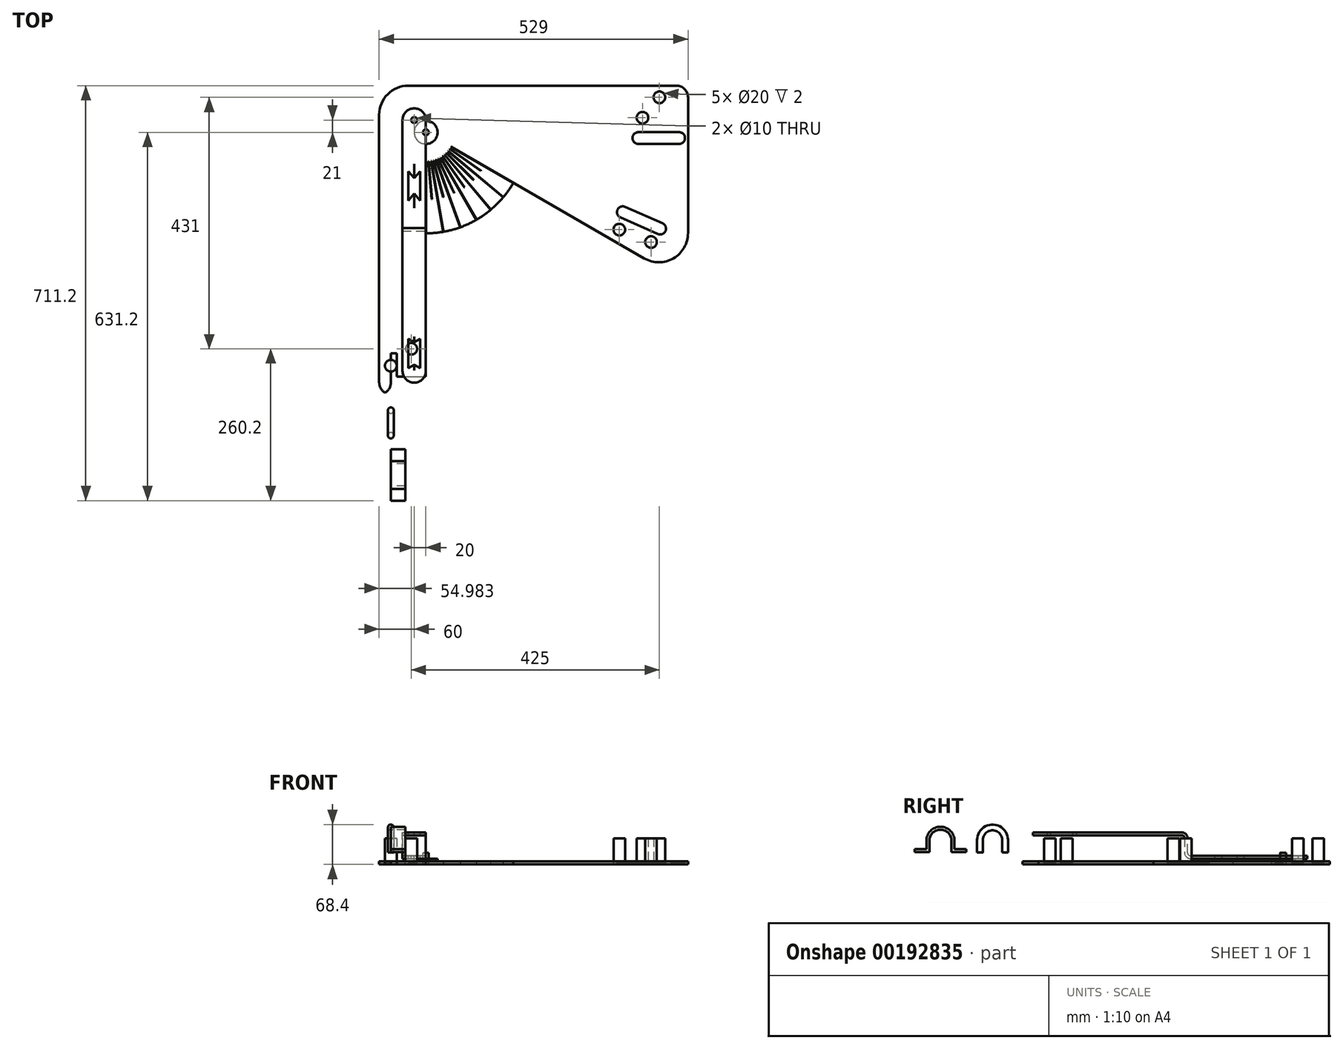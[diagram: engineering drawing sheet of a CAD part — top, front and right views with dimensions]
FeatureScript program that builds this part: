
annotation { "Feature Type Name" : "Feature", "Feature Type Description" : "" }
export const myFeature = defineFeature(function(context is Context, id is Id, definition is map)
    precondition{}
    {
        {
            var Q0;
            Q0=qCreatedBy(makeId("Top.planeOp"),FACE);
            var sketch = newSketch(context, id + "F0", { "sketchPlane" : qUnion([Q0])});
            skLineSegment(sketch, "E0.bottom", {"start": v(0, 0) * mm, "end": v(489, 0) * mm});
            skLineSegment(sketch, "E0.left", {"start": v(0, 0) * mm, "end": v(0, 500) * mm});
            skLineSegment(sketch, "E0.right", {"start": v(489, 0) * mm, "end": v(489, 479) * mm});
            skLineSegment(sketch, "E1.top", {"start": v(0, 0) * mm, "end": v(10, 0) * mm});
            skLineSegment(sketch, "E1.left", {"start": v(0, 489) * mm, "end": v(0, 0) * mm});
            skLineSegment(sketch, "E1.right", {"start": v(10, 50) * mm, "end": v(10, 10) * mm});
            skPoint(sketch, "E2", {"position": v(60, 429) * mm});
            skLineSegment(sketch, "E3", {"start": v(60, 255.9) * mm, "end": v(60, 0) * mm});
            skLineSegment(sketch, "E4", {"start": v(209.9, 342.45) * mm, "end": v(489, 181.32) * mm});
            skLineSegment(sketch, "E5.bottom", {"start": v(10, 48) * mm, "end": v(60, 48) * mm, "construction": true});
            skLineSegment(sketch, "E5.right", {"start": v(60, 48) * mm, "end": v(60, 10) * mm, "construction": true});
            skLineSegment(sketch, "E6.top", {"start": v(441, 429) * mm, "end": v(479, 429) * mm, "construction": true});
            skLineSegment(sketch, "E6.left", {"start": v(441, 479) * mm, "end": v(441, 429) * mm, "construction": true});
            skArc(sketch, "E7", {"start": v(60, 29) * mm, "mid": v(342.84, 146.16) * mm, "end": v(460, 429) * mm, "construction": true});
            skPoint(sketch, "E8", {"position": v(10, 29) * mm});
            skPoint(sketch, "E9", {"position": v(460, 479) * mm});
            skArc(sketch, "E10.0", {"start": v(60, 10) * mm, "mid": v(356.28, 132.72) * mm, "end": v(479, 429) * mm, "construction": true});
            skArc(sketch, "E11.0", {"start": v(60, 48) * mm, "mid": v(329.4, 159.6) * mm, "end": v(441, 429) * mm, "construction": true});
            skLineSegment(sketch, "E12", {"start": v(60, 255.9) * mm, "end": v(209.9, 342.45) * mm, "construction": true});
            skPoint(sketch, "E13.end.orphan", {"position": v(189.9, 354) * mm});
            skPoint(sketch, "E13.start.orphan", {"position": v(60, 279) * mm});
            skCircle(sketch, "E14", {"center": v(60, 429) * mm, "radius": 5 * mm});
            skLineSegment(sketch, "E15.top", {"start": v(489, 489) * mm, "end": v(0, 489) * mm});
            skLineSegment(sketch, "E15.left", {"start": v(489, 479) * mm, "end": v(489, 489) * mm});
            skLineSegment(sketch, "E16", {"start": v(439, 489) * mm, "end": v(439, 479) * mm});
            skLineSegment(sketch, "E17", {"start": v(439, 479) * mm, "end": v(479, 479) * mm});
            skLineSegment(sketch, "E18", {"start": v(479, 479) * mm, "end": v(479, 429) * mm});
            skLineSegment(sketch, "E19", {"start": v(489, 429) * mm, "end": v(479, 429) * mm});
            skArc(sketch, "E20", {"start": v(60, 255.9) * mm, "mid": v(146.55, 279.1) * mm, "end": v(209.9, 342.45) * mm});
            skLineSegment(sketch, "E21", {"start": v(0, 50) * mm, "end": v(10, 50) * mm});
            skLineSegment(sketch, "E22", {"start": v(10, 10) * mm, "end": v(60, 10) * mm});
            skLineSegment(sketch, "E23", {"start": v(60, 0) * mm, "end": v(60, -20) * mm});
            skLineSegment(sketch, "E24", {"start": v(60, -20) * mm, "end": v(0, -20) * mm});
            skLineSegment(sketch, "E25", {"start": v(0, -20) * mm, "end": v(0, 0) * mm});
            skLineSegment(sketch, "E26", {"start": v(0, 489) * mm, "end": v(-20, 489) * mm});
            skLineSegment(sketch, "E27", {"start": v(-20, 489) * mm, "end": v(-20, -20) * mm});
            skLineSegment(sketch, "E28", {"start": v(-20, -20) * mm, "end": v(0, -20) * mm});
            skLineSegment(sketch, "E29", {"start": v(489, 181.32) * mm, "end": v(509, 169.77) * mm});
            skLineSegment(sketch, "E30", {"start": v(509, 169.77) * mm, "end": v(509, 489) * mm});
            skLineSegment(sketch, "E31", {"start": v(509, 489) * mm, "end": v(489, 489) * mm});
            skLineSegment(sketch, "E32", {"start": v(509, 489) * mm, "end": v(509, 509) * mm});
            skLineSegment(sketch, "E33", {"start": v(509, 509) * mm, "end": v(-20, 509) * mm});
            skLineSegment(sketch, "E34", {"start": v(-20, 509) * mm, "end": v(-20, 489) * mm});
            skSolve(sketch);
        }
        {
            var Q0;
            {var subQ3=sQuery(id+"F0.wireOp",EDGE,"E1.right");Q0=makeQuery(id+"F0.imprint","IMPRINT",FACE,{"disambiguationData":[TD([[makeQuery(id+"F0.imprint","IMPRINT",EDGE,{"derivedFrom":subQ3}),1.0]])]});}
            var Q1;
            {var subQ2=sQuery(id+"F0.wireOp",EDGE,"E1.top");Q1=makeQuery(id+"F0.imprint","IMPRINT",FACE,{"disambiguationData":[TD([[makeQuery(id+"F0.imprint","IMPRINT",EDGE,{"derivedFrom":subQ2}),1.0]])]});}
            var Q2;
            {var subQ1=sQuery(id+"F0.wireOp",EDGE,"E15.left");Q2=makeQuery(id+"F0.imprint","IMPRINT",FACE,{"disambiguationData":[TD([[makeQuery(id+"F0.imprint","IMPRINT",EDGE,{"derivedFrom":subQ1}),1.0]])]});}
            var Q3;
            {var subQ1=sQuery(id+"F0.wireOp",EDGE,"E25");Q3=makeQuery(id+"F0.imprint","IMPRINT",FACE,{"disambiguationData":[TD([[makeQuery(id+"F0.imprint","IMPRINT",EDGE,{"derivedFrom":subQ1}),1.0]])]});}
            var Q4;
            {var subQ0=sQuery(id+"F0.wireOp",EDGE,"E1.top");Q4=makeQuery(id+"F0.imprint","IMPRINT",FACE,{"disambiguationData":[TD([[makeQuery(id+"F0.imprint","IMPRINT",EDGE,{"derivedFrom":subQ0}),-1.0]])]});}
            var Q5;
            {var subQ3=sQuery(id+"F0.wireOp",EDGE,"E26");Q5=makeQuery(id+"F0.imprint","IMPRINT",FACE,{"disambiguationData":[TD([[makeQuery(id+"F0.imprint","IMPRINT",EDGE,{"derivedFrom":subQ3}),-1.0]])]});}
            var Q6;
            {var subQ1=sQuery(id+"F0.wireOp",EDGE,"E15.left");Q6=makeQuery(id+"F0.imprint","IMPRINT",FACE,{"disambiguationData":[TD([[makeQuery(id+"F0.imprint","IMPRINT",EDGE,{"derivedFrom":subQ1}),-1.0]])]});}
            extrude(context, id + "F1", {"entities" : qUnion([Q0, Q1, Q2, Q3, Q4, Q5, Q6]), "depth" : 5 * mm});
        }
        {
            var Q0;
            Q0=makeQuery(id+"F1.opExtrude","SWEPT_FACE",FACE,{"disambiguationData":[OSD([sQuery(id+"F0.wireOp",EDGE,"E33")])]});
            cPlane(context, id + "F2", {"entities" : qUnion([Q0]), "cplaneType" : CPlaneType.OFFSET, "offset" : 80 * mm, "oppositeDirection" : true, "width" : 150 * mm, "height" : 150 * mm});
        }
        {
            var Q0;
            Q0=qCreatedBy(id+"F2.planeOp",FACE);
            var sketch = newSketch(context, id + "F3", { "sketchPlane" : qUnion([Q0])});
            skLineSegment(sketch, "E35", {"start": v(-60, 20) * mm, "end": v(-60, 0) * mm});
            skLineSegment(sketch, "E36", {"start": v(-60, 20) * mm, "end": v(-65, 20) * mm});
            skLineSegment(sketch, "E37", {"start": v(-65, 20) * mm, "end": v(-65, 10) * mm});
            skLineSegment(sketch, "E38", {"start": v(-65, 10) * mm, "end": v(-80, 10) * mm});
            skLineSegment(sketch, "E39", {"start": v(-80, 10) * mm, "end": v(-80, 5) * mm});
            skLineSegment(sketch, "E40", {"start": v(-80, 5) * mm, "end": v(-65, 5) * mm});
            skLineSegment(sketch, "E41", {"start": v(-65, 5) * mm, "end": v(-65, 0) * mm});
            skLineSegment(sketch, "E42", {"start": v(-65, 0) * mm, "end": v(-60, 0) * mm});
            skSolve(sketch);
        }
        {
            var Q0;
            Q0=qSketchRegion(id+"F3",true);
            var Q1;
            Q1=sQuery(id+"F3.wireOp",EDGE,"E35");
            revolve(context, id + "F4", {"entities" : qUnion([Q0]), "axis" : qUnion([Q1]), "revolveType" : RevolveType.FULL});
        }
        {
            var Q0;
            Q0=makeQuery(id+"F1.opExtrude","CAP_FACE",FACE,{"disambiguationData":[OSD([sQuery(id+"F0.wireOp",EDGE,"E0.bottom"),sQuery(id+"F0.wireOp",EDGE,"E0.top"),sQuery(id+"F0.wireOp",EDGE,"E0.right"),sQuery(id+"F0.wireOp",EDGE,"E1.right"),sQuery(id+"F0.wireOp",EDGE,"E3"),sQuery(id+"F0.wireOp",EDGE,"E4"),sQuery(id+"F0.wireOp",EDGE,"E12"),sQuery(id+"F0.wireOp",EDGE,"E14")])],"isStart":false});
            cPlane(context, id + "F5", {"entities" : qUnion([Q0]), "cplaneType" : CPlaneType.OFFSET, "offset" : 0 * mm, "width" : 150 * mm, "height" : 150 * mm});
        }
        {
            var Q0;
            Q0=qCreatedBy(id+"F5.planeOp",FACE);
            var sketch = newSketch(context, id + "F6", { "sketchPlane" : qUnion([Q0])});
            skCircle(sketch, "E43", {"center": v(34.98, 58) * mm, "radius": 10 * mm});
            skLineSegment(sketch, "E44.bottom", {"start": v(9.98, 10) * mm, "end": v(59.98, 10) * mm, "construction": true});
            skLineSegment(sketch, "E44.top", {"start": v(9.98, 48) * mm, "end": v(59.98, 48) * mm, "construction": true});
            skLineSegment(sketch, "E44.left", {"start": v(9.98, 10) * mm, "end": v(9.98, 48) * mm, "construction": true});
            skLineSegment(sketch, "E44.right", {"start": v(59.98, 10) * mm, "end": v(59.98, 48) * mm, "construction": true});
            skLineSegment(sketch, "E45.bottom", {"start": v(478.98, 479) * mm, "end": v(440.98, 479) * mm, "construction": true});
            skLineSegment(sketch, "E45.top", {"start": v(478.98, 429) * mm, "end": v(440.98, 429) * mm, "construction": true});
            skLineSegment(sketch, "E45.left", {"start": v(478.98, 479) * mm, "end": v(478.98, 429) * mm, "construction": true});
            skLineSegment(sketch, "E45.right", {"start": v(440.98, 479) * mm, "end": v(440.98, 429) * mm, "construction": true});
            skArc(sketch, "E46", {"start": v(59.98, 29) * mm, "mid": v(342.83, 146.16) * mm, "end": v(459.98, 429) * mm, "construction": true});
            skArc(sketch, "E47.0", {"start": v(59.98, 10) * mm, "mid": v(356.26, 132.72) * mm, "end": v(478.98, 429) * mm, "construction": true});
            skArc(sketch, "E48.0", {"start": v(59.98, 48) * mm, "mid": v(329.4, 159.6) * mm, "end": v(440.98, 429) * mm, "construction": true});
            skLineSegment(sketch, "E49", {"start": v(459.98, 429) * mm, "end": v(459.98, 479) * mm, "construction": true});
            skLineSegment(sketch, "E50", {"start": v(59.98, 29) * mm, "end": v(9.98, 29) * mm, "construction": true});
            skCircle(sketch, "E51", {"center": v(430.98, 454) * mm, "radius": 10 * mm});
            skCircle(sketch, "E52", {"center": v(445.6, 241.01) * mm, "radius": 10 * mm});
            skLineSegment(sketch, "E53", {"start": v(445.6, 241.01) * mm, "end": v(391.37, 262.2) * mm, "construction": true});
            skCircle(sketch, "E54", {"center": v(391.37, 262.2) * mm, "radius": 10 * mm});
            skCircle(sketch, "E55.MirrorC", {"center": v(34.98, 0) * mm, "radius": 10 * mm});
            skCircle(sketch, "E56", {"center": v(-0.02, 29) * mm, "radius": 10 * mm});
            skLineSegment(sketch, "E57", {"start": v(34.98, 0) * mm, "end": v(34.98, 48) * mm, "construction": true});
            skCircle(sketch, "E58.MirrorC", {"center": v(488.98, 454) * mm, "radius": 10 * mm});
            skLineSegment(sketch, "E59", {"start": v(430.98, 454) * mm, "end": v(488.98, 454) * mm, "construction": true});
            skCircle(sketch, "E60", {"center": v(459.98, 489) * mm, "radius": 10 * mm});
            skSolve(sketch);
        }
        {
            var Q0;
            Q0=makeQuery(id+"F6.imprint","IMPRINT",FACE,{"disambiguationData":[TD([[makeQuery(id+"F6.imprint","IMPRINT",EDGE,{"derivedFrom":sQuery(id+"F6.wireOp",EDGE,"E58.MirrorC")}),-1.0]])]});
            var Q1;
            Q1=makeQuery(id+"F6.imprint","IMPRINT",FACE,{"disambiguationData":[TD([[makeQuery(id+"F6.imprint","IMPRINT",EDGE,{"derivedFrom":sQuery(id+"F6.wireOp",EDGE,"E60")}),1.0]])]});
            var Q2;
            Q2=makeQuery(id+"F6.imprint","IMPRINT",FACE,{"disambiguationData":[TD([[makeQuery(id+"F6.imprint","IMPRINT",EDGE,{"derivedFrom":sQuery(id+"F6.wireOp",EDGE,"E51")}),1.0]])]});
            var Q3;
            Q3=makeQuery(id+"F6.imprint","IMPRINT",FACE,{"disambiguationData":[TD([[makeQuery(id+"F6.imprint","IMPRINT",EDGE,{"derivedFrom":sQuery(id+"F6.wireOp",EDGE,"E52")}),1.0]])]});
            var Q4;
            Q4=makeQuery(id+"F6.imprint","IMPRINT",FACE,{"disambiguationData":[TD([[makeQuery(id+"F6.imprint","IMPRINT",EDGE,{"derivedFrom":sQuery(id+"F6.wireOp",EDGE,"E54")}),1.0]])]});
            var Q5;
            Q5=makeQuery(id+"F6.imprint","IMPRINT",FACE,{"disambiguationData":[TD([[makeQuery(id+"F6.imprint","IMPRINT",EDGE,{"derivedFrom":sQuery(id+"F6.wireOp",EDGE,"E55.MirrorC")}),-1.0]])]});
            var Q6;
            Q6=makeQuery(id+"F6.imprint","IMPRINT",FACE,{"disambiguationData":[TD([[makeQuery(id+"F6.imprint","IMPRINT",EDGE,{"derivedFrom":sQuery(id+"F6.wireOp",EDGE,"E43")}),1.0]])]});
            var Q7;
            Q7=makeQuery(id+"F6.imprint","IMPRINT",FACE,{"disambiguationData":[TD([[makeQuery(id+"F6.imprint","IMPRINT",EDGE,{"derivedFrom":sQuery(id+"F6.wireOp",EDGE,"E56")}),1.0]])]});
            extrude(context, id + "F7", {"entities" : qUnion([Q0, Q1, Q2, Q3, Q4, Q5, Q6, Q7]), "operationType" : NewBodyOperationType.REMOVE, "oppositeDirection" : true, "depth" : 2 * mm});
        }
        {
            var Q0;
            Q0=makeQuery(id+"F6.imprint","IMPRINT",FACE,{"disambiguationData":[TD([[makeQuery(id+"F6.imprint","IMPRINT",EDGE,{"derivedFrom":sQuery(id+"F6.wireOp",EDGE,"E58.MirrorC")}),-1.0]])]});
            var Q1;
            Q1=makeQuery(id+"F6.imprint","IMPRINT",FACE,{"disambiguationData":[TD([[makeQuery(id+"F6.imprint","IMPRINT",EDGE,{"derivedFrom":sQuery(id+"F6.wireOp",EDGE,"E60")}),1.0]])]});
            var Q2;
            Q2=makeQuery(id+"F6.imprint","IMPRINT",FACE,{"disambiguationData":[TD([[makeQuery(id+"F6.imprint","IMPRINT",EDGE,{"derivedFrom":sQuery(id+"F6.wireOp",EDGE,"E51")}),1.0]])]});
            var Q3;
            Q3=makeQuery(id+"F6.imprint","IMPRINT",FACE,{"disambiguationData":[TD([[makeQuery(id+"F6.imprint","IMPRINT",EDGE,{"derivedFrom":sQuery(id+"F6.wireOp",EDGE,"E52")}),1.0]])]});
            var Q4;
            Q4=makeQuery(id+"F6.imprint","IMPRINT",FACE,{"disambiguationData":[TD([[makeQuery(id+"F6.imprint","IMPRINT",EDGE,{"derivedFrom":sQuery(id+"F6.wireOp",EDGE,"E54")}),1.0]])]});
            var Q5;
            Q5=makeQuery(id+"F6.imprint","IMPRINT",FACE,{"disambiguationData":[TD([[makeQuery(id+"F6.imprint","IMPRINT",EDGE,{"derivedFrom":sQuery(id+"F6.wireOp",EDGE,"E56")}),1.0]])]});
            var Q6;
            Q6=makeQuery(id+"F6.imprint","IMPRINT",FACE,{"disambiguationData":[TD([[makeQuery(id+"F6.imprint","IMPRINT",EDGE,{"derivedFrom":sQuery(id+"F6.wireOp",EDGE,"E55.MirrorC")}),-1.0]])]});
            var Q7;
            Q7=makeQuery(id+"F6.imprint","IMPRINT",FACE,{"disambiguationData":[TD([[makeQuery(id+"F6.imprint","IMPRINT",EDGE,{"derivedFrom":sQuery(id+"F6.wireOp",EDGE,"E43")}),1.0]])]});
            extrude(context, id + "F8", {"entities" : qUnion([Q0, Q1, Q2, Q3, Q4, Q5, Q6, Q7]), "depth" : 40 * mm});
        }
        {
            var Q0;
            Q0=makeQuery(id+"F1.opExtrude","CAP_FACE",FACE,{"disambiguationData":[OSD([sQuery(id+"F0.wireOp",EDGE,"E0.bottom"),sQuery(id+"F0.wireOp",EDGE,"E0.right"),sQuery(id+"F0.wireOp",EDGE,"E1.right"),sQuery(id+"F0.wireOp",EDGE,"E3"),sQuery(id+"F0.wireOp",EDGE,"E4"),sQuery(id+"F0.wireOp",EDGE,"E12"),sQuery(id+"F0.wireOp",EDGE,"E14"),sQuery(id+"F0.wireOp",EDGE,"E15.top"),sQuery(id+"F0.wireOp",EDGE,"E16"),sQuery(id+"F0.wireOp",EDGE,"E17"),sQuery(id+"F0.wireOp",EDGE,"E18"),sQuery(id+"F0.wireOp",EDGE,"E19")])],"isStart":false});
            var sketch = newSketch(context, id + "F9", { "sketchPlane" : qUnion([Q0])});
            skLineSegment(sketch, "E61", {"start": v(60, 379) * mm, "end": v(60, 255.9) * mm});
            skLineSegment(sketch, "E62", {"start": v(103.3, 404) * mm, "end": v(209.9, 342.45) * mm});
            skArc(sketch, "E63", {"start": v(60, 314) * mm, "mid": v(117.5, 329.4) * mm, "end": v(159.6, 371.5) * mm});
            skLineSegment(sketch, "E64.0", {"start": v(64.45, 426.72) * mm, "end": v(210.03, 342.67) * mm});
            skArc(sketch, "E65", {"start": v(60, 424) * mm, "mid": v(62.6, 424.73) * mm, "end": v(64.45, 426.72) * mm});
            skLineSegment(sketch, "E66.trimOffspring", {"start": v(64.2, 426.29) * mm, "end": v(64.83, 425.92) * mm});
            skLineSegment(sketch, "E67", {"start": v(210.03, 342.67) * mm, "end": v(209.9, 342.45) * mm});
            skLineSegment(sketch, "E68", {"start": v(100.96, 400.32) * mm, "end": v(154.2, 363.04) * mm});
            skLineSegment(sketch, "E69", {"start": v(98.3, 396.86) * mm, "end": v(192.6, 317.74) * mm});
            skLineSegment(sketch, "E70", {"start": v(95.36, 393.64) * mm, "end": v(141.32, 347.68) * mm});
            skLineSegment(sketch, "E71", {"start": v(92.14, 390.7) * mm, "end": v(171.26, 296.4) * mm});
            skLineSegment(sketch, "E72", {"start": v(88.68, 388.04) * mm, "end": v(125.96, 334.8) * mm});
            skLineSegment(sketch, "E73", {"start": v(85, 385.7) * mm, "end": v(146.55, 279.1) * mm});
            skLineSegment(sketch, "E74", {"start": v(81.13, 383.68) * mm, "end": v(108.6, 324.77) * mm});
            skLineSegment(sketch, "E75", {"start": v(77.1, 382.02) * mm, "end": v(119.2, 266.34) * mm});
            skLineSegment(sketch, "E76", {"start": v(72.94, 380.7) * mm, "end": v(89.76, 317.92) * mm});
            skLineSegment(sketch, "E77", {"start": v(68.68, 379.76) * mm, "end": v(90.06, 258.54) * mm});
            skLineSegment(sketch, "E78", {"start": v(64.36, 379.2) * mm, "end": v(70.02, 314.44) * mm});
            skArc(sketch, "E79", {"start": v(60, 255.9) * mm, "mid": v(146.55, 279.1) * mm, "end": v(209.9, 342.45) * mm, "construction": true});
            skPoint(sketch, "E80.orphan", {"position": v(117.5, 329.4) * mm});
            skLineSegment(sketch, "E81.0", {"start": v(64.24, 426.34) * mm, "end": v(64.83, 425.92) * mm});
            skLineSegment(sketch, "E82.0", {"start": v(63.95, 425.93) * mm, "end": v(64.55, 425.51) * mm});
            skLineSegment(sketch, "E83.0", {"start": v(63.67, 425.6) * mm, "end": v(64.23, 425.13) * mm});
            skLineSegment(sketch, "E84.0", {"start": v(64, 425.98) * mm, "end": v(64.55, 425.51) * mm});
            skLineSegment(sketch, "E85.0", {"start": v(63.36, 425.29) * mm, "end": v(63.87, 424.77) * mm});
            skLineSegment(sketch, "E86.0", {"start": v(63.71, 425.64) * mm, "end": v(64.23, 425.13) * mm});
            skLineSegment(sketch, "E87.0", {"start": v(63.02, 425) * mm, "end": v(63.49, 424.45) * mm});
            skLineSegment(sketch, "E88.0", {"start": v(63.4, 425.33) * mm, "end": v(63.87, 424.77) * mm});
            skLineSegment(sketch, "E89.0", {"start": v(63.07, 425.05) * mm, "end": v(63.49, 424.45) * mm});
            skLineSegment(sketch, "E90.0", {"start": v(62.66, 424.76) * mm, "end": v(63.08, 424.17) * mm});
            skLineSegment(sketch, "E91.0", {"start": v(55.7, 435.96) * mm, "end": v(62.65, 423.92) * mm});
            skLineSegment(sketch, "E92.0", {"start": v(56.12, 436.21) * mm, "end": v(63.08, 424.17) * mm});
            skLineSegment(sketch, "E93.0", {"start": v(61.89, 424.36) * mm, "end": v(62.2, 423.7) * mm});
            skLineSegment(sketch, "E94.0", {"start": v(62.34, 424.57) * mm, "end": v(62.65, 423.92) * mm});
            skLineSegment(sketch, "E95.0", {"start": v(61.48, 424.22) * mm, "end": v(61.72, 423.53) * mm});
            skLineSegment(sketch, "E96.0", {"start": v(61.95, 424.39) * mm, "end": v(62.2, 423.7) * mm});
            skLineSegment(sketch, "E97.0", {"start": v(61.05, 424.1) * mm, "end": v(61.24, 423.4) * mm});
            skLineSegment(sketch, "E98.0", {"start": v(61.54, 424.24) * mm, "end": v(61.72, 423.53) * mm});
            skLineSegment(sketch, "E99.0", {"start": v(60.62, 424.03) * mm, "end": v(60.75, 423.32) * mm});
            skLineSegment(sketch, "E100.0", {"start": v(61.11, 424.12) * mm, "end": v(61.24, 423.4) * mm});
            skLineSegment(sketch, "E101.0", {"start": v(60.19, 424) * mm, "end": v(60.25, 423.27) * mm});
            skLineSegment(sketch, "E102.0", {"start": v(60.68, 424.04) * mm, "end": v(60.75, 423.32) * mm});
            skLineSegment(sketch, "E103.0", {"start": v(59.75, 429) * mm, "end": v(59.75, 255.9) * mm});
            skLineSegment(sketch, "E104.0", {"start": v(60.25, 424) * mm, "end": v(60.25, 423.27) * mm});
            skArc(sketch, "E105", {"start": v(103.3, 404) * mm, "mid": v(85, 385.7) * mm, "end": v(60, 379) * mm});
            skLineSegment(sketch, "E106.trimOffspring", {"start": v(60.25, 379) * mm, "end": v(60.25, 255.9) * mm});
            skLineSegment(sketch, "E107.trimOffspring", {"start": v(64.1, 379.17) * mm, "end": v(69.77, 314.42) * mm});
            skLineSegment(sketch, "E108.trimOffspring", {"start": v(64.6, 379.21) * mm, "end": v(70.27, 314.46) * mm});
            skLineSegment(sketch, "E109.trimOffspring", {"start": v(68.44, 379.72) * mm, "end": v(89.81, 258.5) * mm});
            skLineSegment(sketch, "E110.trimOffspring", {"start": v(68.93, 379.8) * mm, "end": v(90.3, 258.58) * mm});
            skLineSegment(sketch, "E111.trimOffspring", {"start": v(72.7, 380.64) * mm, "end": v(89.52, 317.85) * mm});
            skLineSegment(sketch, "E112.trimOffspring", {"start": v(73.18, 380.77) * mm, "end": v(90, 317.98) * mm});
            skLineSegment(sketch, "E113.trimOffspring", {"start": v(76.87, 381.93) * mm, "end": v(118.97, 266.26) * mm});
            skLineSegment(sketch, "E114.trimOffspring", {"start": v(77.34, 382.1) * mm, "end": v(119.44, 266.43) * mm});
            skLineSegment(sketch, "E115.trimOffspring", {"start": v(80.9, 383.58) * mm, "end": v(108.37, 324.67) * mm});
            skLineSegment(sketch, "E116.trimOffspring", {"start": v(81.36, 383.8) * mm, "end": v(108.83, 324.88) * mm});
            skLineSegment(sketch, "E117.trimOffspring", {"start": v(88.47, 387.9) * mm, "end": v(125.76, 334.65) * mm});
            skLineSegment(sketch, "E118.trimOffspring", {"start": v(88.88, 388.19) * mm, "end": v(126.17, 334.94) * mm});
            skLineSegment(sketch, "E119.trimOffspring", {"start": v(84.78, 385.57) * mm, "end": v(146.33, 278.97) * mm});
            skLineSegment(sketch, "E120.trimOffspring", {"start": v(85.22, 385.82) * mm, "end": v(146.76, 279.22) * mm});
            skLineSegment(sketch, "E121.trimOffspring", {"start": v(91.95, 390.54) * mm, "end": v(171.07, 296.24) * mm});
            skLineSegment(sketch, "E122.trimOffspring", {"start": v(92.33, 390.86) * mm, "end": v(171.45, 296.56) * mm});
            skLineSegment(sketch, "E123.trimOffspring", {"start": v(95.18, 393.47) * mm, "end": v(141.14, 347.5) * mm});
            skLineSegment(sketch, "E124.trimOffspring", {"start": v(95.53, 393.82) * mm, "end": v(141.5, 347.86) * mm});
            skLineSegment(sketch, "E125.trimOffspring", {"start": v(98.14, 396.67) * mm, "end": v(192.44, 317.55) * mm});
            skLineSegment(sketch, "E126.trimOffspring", {"start": v(98.46, 397.05) * mm, "end": v(192.76, 317.93) * mm});
            skLineSegment(sketch, "E127.trimOffspring", {"start": v(100.81, 400.12) * mm, "end": v(154.06, 362.83) * mm});
            skLineSegment(sketch, "E128.trimOffspring", {"start": v(101.1, 400.53) * mm, "end": v(154.35, 363.24) * mm});
            skLineSegment(sketch, "E129.trimOffspring", {"start": v(103.18, 403.78) * mm, "end": v(209.78, 342.24) * mm});
            skArc(sketch, "E130", {"start": v(209.9, 342.45) * mm, "mid": v(146.55, 279.1) * mm, "end": v(60, 255.9) * mm});
            skSolve(sketch);
        }
        {
            var Q0;
            {var subQ0=sQuery(id+"F9.wireOp",EDGE,"E105");var subQ1=sQuery(id+"F9.wireOp",EDGE,"E62");var subQ2=makeQuery(id+"F9.imprint","INTERSECT",VERTEX,{"derivedFrom":[subQ1,subQ0]});Q0=makeQuery(id+"F9.imprint","IMPRINT",FACE,{"disambiguationData":[TD([[makeQuery(id+"F9.imprint","IMPRINT",EDGE,{"disambiguationData":[TD([[subQ2,-1.0]])],"derivedFrom":subQ1}),-1.0]])]});}
            var Q1;
            {var subQ0=sQuery(id+"F9.wireOp",EDGE,"E62");var subQ3=sQuery(id+"F9.wireOp",EDGE,"E63");var subQ4=makeQuery(id+"F9.imprint","INTERSECT",VERTEX,{"derivedFrom":[subQ0,subQ3]});Q1=makeQuery(id+"F9.imprint","IMPRINT",FACE,{"disambiguationData":[TD([[makeQuery(id+"F9.imprint","IMPRINT",EDGE,{"disambiguationData":[TD([[subQ4,1.0]])],"derivedFrom":subQ3}),-1.0]])]});}
            var Q2;
            {var subQ0=sQuery(id+"F9.wireOp",EDGE,"E68");Q2=makeQuery(id+"F9.imprint","IMPRINT",FACE,{"disambiguationData":[TD([[makeQuery(id+"F9.imprint","IMPRINT",EDGE,{"derivedFrom":subQ0}),1.0]])]});}
            var Q3;
            {var subQ0=sQuery(id+"F9.wireOp",EDGE,"E68");Q3=makeQuery(id+"F9.imprint","IMPRINT",FACE,{"disambiguationData":[TD([[makeQuery(id+"F9.imprint","IMPRINT",EDGE,{"derivedFrom":subQ0}),-1.0]])]});}
            var Q4;
            {var subQ0=sQuery(id+"F9.wireOp",EDGE,"E69");var subQ1=sQuery(id+"F9.wireOp",EDGE,"E63");var subQ2=makeQuery(id+"F9.imprint","INTERSECT",VERTEX,{"derivedFrom":[subQ1,subQ0]});Q4=makeQuery(id+"F9.imprint","IMPRINT",FACE,{"disambiguationData":[TD([[makeQuery(id+"F9.imprint","IMPRINT",EDGE,{"disambiguationData":[TD([[subQ2,-1.0]])],"derivedFrom":subQ1}),1.0]])]});}
            var Q5;
            {var subQ0=sQuery(id+"F9.wireOp",EDGE,"E125.trimOffspring");var subQ1=sQuery(id+"F9.wireOp",EDGE,"E63");var subQ2=makeQuery(id+"F9.imprint","INTERSECT",VERTEX,{"derivedFrom":[subQ1,subQ0]});Q5=makeQuery(id+"F9.imprint","IMPRINT",FACE,{"disambiguationData":[TD([[makeQuery(id+"F9.imprint","IMPRINT",EDGE,{"disambiguationData":[TD([[subQ2,-1.0]])],"derivedFrom":subQ1}),1.0]])]});}
            var Q6;
            {var subQ0=sQuery(id+"F9.wireOp",EDGE,"E125.trimOffspring");var subQ1=sQuery(id+"F9.wireOp",EDGE,"E63");var subQ2=makeQuery(id+"F9.imprint","INTERSECT",VERTEX,{"derivedFrom":[subQ1,subQ0]});Q6=makeQuery(id+"F9.imprint","IMPRINT",FACE,{"disambiguationData":[TD([[makeQuery(id+"F9.imprint","IMPRINT",EDGE,{"disambiguationData":[TD([[subQ2,-1.0]])],"derivedFrom":subQ1}),-1.0]])]});}
            var Q7;
            {var subQ0=sQuery(id+"F9.wireOp",EDGE,"E69");var subQ1=sQuery(id+"F9.wireOp",EDGE,"E63");var subQ2=makeQuery(id+"F9.imprint","INTERSECT",VERTEX,{"derivedFrom":[subQ1,subQ0]});Q7=makeQuery(id+"F9.imprint","IMPRINT",FACE,{"disambiguationData":[TD([[makeQuery(id+"F9.imprint","IMPRINT",EDGE,{"disambiguationData":[TD([[subQ2,-1.0]])],"derivedFrom":subQ1}),-1.0]])]});}
            var Q8;
            {var subQ0=sQuery(id+"F9.wireOp",EDGE,"E70");Q8=makeQuery(id+"F9.imprint","IMPRINT",FACE,{"disambiguationData":[TD([[makeQuery(id+"F9.imprint","IMPRINT",EDGE,{"derivedFrom":subQ0}),-1.0]])]});}
            var Q9;
            {var subQ0=sQuery(id+"F9.wireOp",EDGE,"E70");Q9=makeQuery(id+"F9.imprint","IMPRINT",FACE,{"disambiguationData":[TD([[makeQuery(id+"F9.imprint","IMPRINT",EDGE,{"derivedFrom":subQ0}),1.0]])]});}
            var Q10;
            {var subQ0=sQuery(id+"F9.wireOp",EDGE,"E71");var subQ1=sQuery(id+"F9.wireOp",EDGE,"E63");var subQ2=makeQuery(id+"F9.imprint","INTERSECT",VERTEX,{"derivedFrom":[subQ1,subQ0]});Q10=makeQuery(id+"F9.imprint","IMPRINT",FACE,{"disambiguationData":[TD([[makeQuery(id+"F9.imprint","IMPRINT",EDGE,{"disambiguationData":[TD([[subQ2,-1.0]])],"derivedFrom":subQ1}),1.0]])]});}
            var Q11;
            {var subQ0=sQuery(id+"F9.wireOp",EDGE,"E71");var subQ1=sQuery(id+"F9.wireOp",EDGE,"E63");var subQ2=makeQuery(id+"F9.imprint","INTERSECT",VERTEX,{"derivedFrom":[subQ1,subQ0]});Q11=makeQuery(id+"F9.imprint","IMPRINT",FACE,{"disambiguationData":[TD([[makeQuery(id+"F9.imprint","IMPRINT",EDGE,{"disambiguationData":[TD([[subQ2,-1.0]])],"derivedFrom":subQ1}),-1.0]])]});}
            var Q12;
            {var subQ0=sQuery(id+"F9.wireOp",EDGE,"E121.trimOffspring");var subQ1=sQuery(id+"F9.wireOp",EDGE,"E63");var subQ2=makeQuery(id+"F9.imprint","INTERSECT",VERTEX,{"derivedFrom":[subQ1,subQ0]});Q12=makeQuery(id+"F9.imprint","IMPRINT",FACE,{"disambiguationData":[TD([[makeQuery(id+"F9.imprint","IMPRINT",EDGE,{"disambiguationData":[TD([[subQ2,-1.0]])],"derivedFrom":subQ1}),-1.0]])]});}
            var Q13;
            {var subQ0=sQuery(id+"F9.wireOp",EDGE,"E121.trimOffspring");var subQ1=sQuery(id+"F9.wireOp",EDGE,"E63");var subQ2=makeQuery(id+"F9.imprint","INTERSECT",VERTEX,{"derivedFrom":[subQ1,subQ0]});Q13=makeQuery(id+"F9.imprint","IMPRINT",FACE,{"disambiguationData":[TD([[makeQuery(id+"F9.imprint","IMPRINT",EDGE,{"disambiguationData":[TD([[subQ2,-1.0]])],"derivedFrom":subQ1}),1.0]])]});}
            var Q14;
            {var subQ0=sQuery(id+"F9.wireOp",EDGE,"E72");Q14=makeQuery(id+"F9.imprint","IMPRINT",FACE,{"disambiguationData":[TD([[makeQuery(id+"F9.imprint","IMPRINT",EDGE,{"derivedFrom":subQ0}),1.0]])]});}
            var Q15;
            {var subQ0=sQuery(id+"F9.wireOp",EDGE,"E72");Q15=makeQuery(id+"F9.imprint","IMPRINT",FACE,{"disambiguationData":[TD([[makeQuery(id+"F9.imprint","IMPRINT",EDGE,{"derivedFrom":subQ0}),-1.0]])]});}
            var Q16;
            {var subQ0=sQuery(id+"F9.wireOp",EDGE,"E120.trimOffspring");var subQ1=sQuery(id+"F9.wireOp",EDGE,"E63");var subQ2=makeQuery(id+"F9.imprint","INTERSECT",VERTEX,{"derivedFrom":[subQ1,subQ0]});Q16=makeQuery(id+"F9.imprint","IMPRINT",FACE,{"disambiguationData":[TD([[makeQuery(id+"F9.imprint","IMPRINT",EDGE,{"disambiguationData":[TD([[subQ2,1.0]])],"derivedFrom":subQ1}),1.0]])]});}
            var Q17;
            {var subQ0=sQuery(id+"F9.wireOp",EDGE,"E119.trimOffspring");var subQ1=sQuery(id+"F9.wireOp",EDGE,"E63");var subQ2=makeQuery(id+"F9.imprint","INTERSECT",VERTEX,{"derivedFrom":[subQ1,subQ0]});Q17=makeQuery(id+"F9.imprint","IMPRINT",FACE,{"disambiguationData":[TD([[makeQuery(id+"F9.imprint","IMPRINT",EDGE,{"disambiguationData":[TD([[subQ2,-1.0]])],"derivedFrom":subQ1}),1.0]])]});}
            var Q18;
            {var subQ0=sQuery(id+"F9.wireOp",EDGE,"E74");Q18=makeQuery(id+"F9.imprint","IMPRINT",FACE,{"disambiguationData":[TD([[makeQuery(id+"F9.imprint","IMPRINT",EDGE,{"derivedFrom":subQ0}),-1.0]])]});}
            var Q19;
            {var subQ0=sQuery(id+"F9.wireOp",EDGE,"E74");Q19=makeQuery(id+"F9.imprint","IMPRINT",FACE,{"disambiguationData":[TD([[makeQuery(id+"F9.imprint","IMPRINT",EDGE,{"derivedFrom":subQ0}),1.0]])]});}
            var Q20;
            {var subQ0=sQuery(id+"F9.wireOp",EDGE,"E75");var subQ1=sQuery(id+"F9.wireOp",EDGE,"E63");var subQ2=makeQuery(id+"F9.imprint","INTERSECT",VERTEX,{"derivedFrom":[subQ1,subQ0]});Q20=makeQuery(id+"F9.imprint","IMPRINT",FACE,{"disambiguationData":[TD([[makeQuery(id+"F9.imprint","IMPRINT",EDGE,{"disambiguationData":[TD([[subQ2,-1.0]])],"derivedFrom":subQ1}),1.0]])]});}
            var Q21;
            {var subQ0=sQuery(id+"F9.wireOp",EDGE,"E113.trimOffspring");var subQ1=sQuery(id+"F9.wireOp",EDGE,"E63");var subQ2=makeQuery(id+"F9.imprint","INTERSECT",VERTEX,{"derivedFrom":[subQ1,subQ0]});Q21=makeQuery(id+"F9.imprint","IMPRINT",FACE,{"disambiguationData":[TD([[makeQuery(id+"F9.imprint","IMPRINT",EDGE,{"disambiguationData":[TD([[subQ2,-1.0]])],"derivedFrom":subQ1}),1.0]])]});}
            var Q22;
            {var subQ0=sQuery(id+"F9.wireOp",EDGE,"E113.trimOffspring");var subQ1=sQuery(id+"F9.wireOp",EDGE,"E63");var subQ2=makeQuery(id+"F9.imprint","INTERSECT",VERTEX,{"derivedFrom":[subQ1,subQ0]});Q22=makeQuery(id+"F9.imprint","IMPRINT",FACE,{"disambiguationData":[TD([[makeQuery(id+"F9.imprint","IMPRINT",EDGE,{"disambiguationData":[TD([[subQ2,-1.0]])],"derivedFrom":subQ1}),-1.0]])]});}
            var Q23;
            {var subQ0=sQuery(id+"F9.wireOp",EDGE,"E75");var subQ1=sQuery(id+"F9.wireOp",EDGE,"E63");var subQ2=makeQuery(id+"F9.imprint","INTERSECT",VERTEX,{"derivedFrom":[subQ1,subQ0]});Q23=makeQuery(id+"F9.imprint","IMPRINT",FACE,{"disambiguationData":[TD([[makeQuery(id+"F9.imprint","IMPRINT",EDGE,{"disambiguationData":[TD([[subQ2,-1.0]])],"derivedFrom":subQ1}),-1.0]])]});}
            var Q24;
            {var subQ0=sQuery(id+"F9.wireOp",EDGE,"E76");Q24=makeQuery(id+"F9.imprint","IMPRINT",FACE,{"disambiguationData":[TD([[makeQuery(id+"F9.imprint","IMPRINT",EDGE,{"derivedFrom":subQ0}),1.0]])]});}
            var Q25;
            {var subQ0=sQuery(id+"F9.wireOp",EDGE,"E76");Q25=makeQuery(id+"F9.imprint","IMPRINT",FACE,{"disambiguationData":[TD([[makeQuery(id+"F9.imprint","IMPRINT",EDGE,{"derivedFrom":subQ0}),-1.0]])]});}
            var Q26;
            {var subQ0=sQuery(id+"F9.wireOp",EDGE,"E77");var subQ1=sQuery(id+"F9.wireOp",EDGE,"E63");var subQ2=makeQuery(id+"F9.imprint","INTERSECT",VERTEX,{"derivedFrom":[subQ1,subQ0]});Q26=makeQuery(id+"F9.imprint","IMPRINT",FACE,{"disambiguationData":[TD([[makeQuery(id+"F9.imprint","IMPRINT",EDGE,{"disambiguationData":[TD([[subQ2,-1.0]])],"derivedFrom":subQ1}),1.0]])]});}
            var Q27;
            {var subQ0=sQuery(id+"F9.wireOp",EDGE,"E109.trimOffspring");var subQ1=sQuery(id+"F9.wireOp",EDGE,"E63");var subQ2=makeQuery(id+"F9.imprint","INTERSECT",VERTEX,{"derivedFrom":[subQ1,subQ0]});Q27=makeQuery(id+"F9.imprint","IMPRINT",FACE,{"disambiguationData":[TD([[makeQuery(id+"F9.imprint","IMPRINT",EDGE,{"disambiguationData":[TD([[subQ2,-1.0]])],"derivedFrom":subQ1}),1.0]])]});}
            var Q28;
            {var subQ0=sQuery(id+"F9.wireOp",EDGE,"E109.trimOffspring");var subQ1=sQuery(id+"F9.wireOp",EDGE,"E63");var subQ2=makeQuery(id+"F9.imprint","INTERSECT",VERTEX,{"derivedFrom":[subQ1,subQ0]});Q28=makeQuery(id+"F9.imprint","IMPRINT",FACE,{"disambiguationData":[TD([[makeQuery(id+"F9.imprint","IMPRINT",EDGE,{"disambiguationData":[TD([[subQ2,-1.0]])],"derivedFrom":subQ1}),-1.0]])]});}
            var Q29;
            {var subQ0=sQuery(id+"F9.wireOp",EDGE,"E77");var subQ1=sQuery(id+"F9.wireOp",EDGE,"E63");var subQ2=makeQuery(id+"F9.imprint","INTERSECT",VERTEX,{"derivedFrom":[subQ1,subQ0]});Q29=makeQuery(id+"F9.imprint","IMPRINT",FACE,{"disambiguationData":[TD([[makeQuery(id+"F9.imprint","IMPRINT",EDGE,{"disambiguationData":[TD([[subQ2,-1.0]])],"derivedFrom":subQ1}),-1.0]])]});}
            var Q30;
            {var subQ0=sQuery(id+"F9.wireOp",EDGE,"E78");Q30=makeQuery(id+"F9.imprint","IMPRINT",FACE,{"disambiguationData":[TD([[makeQuery(id+"F9.imprint","IMPRINT",EDGE,{"derivedFrom":subQ0}),1.0]])]});}
            var Q31;
            {var subQ0=sQuery(id+"F9.wireOp",EDGE,"E78");Q31=makeQuery(id+"F9.imprint","IMPRINT",FACE,{"disambiguationData":[TD([[makeQuery(id+"F9.imprint","IMPRINT",EDGE,{"derivedFrom":subQ0}),-1.0]])]});}
            var Q32;
            {var subQ6=sQuery(id+"F9.wireOp",EDGE,"E61");Q32=makeQuery(id+"F9.imprint","IMPRINT",FACE,{"disambiguationData":[TD([[makeQuery(id+"F9.imprint","IMPRINT",EDGE,{"derivedFrom":subQ6}),1.0]])]});}
            var Q33;
            {var subQ0=sQuery(id+"F9.wireOp",EDGE,"E119.trimOffspring");var subQ1=sQuery(id+"F9.wireOp",EDGE,"E63");var subQ2=makeQuery(id+"F9.imprint","INTERSECT",VERTEX,{"derivedFrom":[subQ1,subQ0]});Q33=makeQuery(id+"F9.imprint","IMPRINT",FACE,{"disambiguationData":[TD([[makeQuery(id+"F9.imprint","IMPRINT",EDGE,{"disambiguationData":[TD([[subQ2,-1.0]])],"derivedFrom":subQ1}),-1.0]])]});}
            var Q34;
            {var subQ0=sQuery(id+"F9.wireOp",EDGE,"E73");var subQ1=sQuery(id+"F9.wireOp",EDGE,"E63");var subQ2=makeQuery(id+"F9.imprint","INTERSECT",VERTEX,{"derivedFrom":[subQ1,subQ0]});Q34=makeQuery(id+"F9.imprint","IMPRINT",FACE,{"disambiguationData":[TD([[makeQuery(id+"F9.imprint","IMPRINT",EDGE,{"disambiguationData":[TD([[subQ2,-1.0]])],"derivedFrom":subQ1}),-1.0]])]});}
            extrude(context, id + "F10", {"entities" : qUnion([Q0, Q1, Q2, Q3, Q4, Q5, Q6, Q7, Q8, Q9, Q10, Q11, Q12, Q13, Q14, Q15, Q16, Q17, Q18, Q19, Q20, Q21, Q22, Q23, Q24, Q25, Q26, Q27, Q28, Q29, Q30, Q31, Q32, Q33, Q34]), "operationType" : NewBodyOperationType.REMOVE, "oppositeDirection" : true, "depth" : 0.5 * mm});
        }
        {
            var Q0;
            Q0=makeQuery(id+"F10.boolean.opBoolean","MERGE",FACE,{"derivedFrom":[makeQuery(id+"F1.opExtrude","SWEPT_FACE",FACE,{"disambiguationData":[OSD([sQuery(id+"F0.wireOp",EDGE,"E3")])]}),makeQuery(id+"F10.opExtrude","SWEPT_FACE",FACE,{"disambiguationData":[OSD([sQuery(id+"F9.wireOp",EDGE,"E61")])]})]});
            var sketch = newSketch(context, id + "F11", { "sketchPlane" : qUnion([Q0])});
            skLineSegment(sketch, "E131.bottom", {"start": v(470, 10) * mm, "end": v(260, 10) * mm});
            skLineSegment(sketch, "E131.top", {"start": v(470, 15) * mm, "end": v(265, 15) * mm});
            skLineSegment(sketch, "E131.left", {"start": v(470, 10) * mm, "end": v(470, 15) * mm});
            skLineSegment(sketch, "E132", {"start": v(265, 15) * mm, "end": v(265, 55) * mm});
            skLineSegment(sketch, "E133", {"start": v(265, 55) * mm, "end": v(0, 55) * mm});
            skLineSegment(sketch, "E134", {"start": v(0, 55) * mm, "end": v(0, 50) * mm});
            skLineSegment(sketch, "E135", {"start": v(0, 50) * mm, "end": v(260, 50) * mm});
            skLineSegment(sketch, "E136", {"start": v(260, 50) * mm, "end": v(260, 10) * mm});
            skPoint(sketch, "E137.trimOffspring.end.orphan", {"position": v(0, 35) * mm});
            skSolve(sketch);
        }
        {
            var Q0;
            Q0=qSketchRegion(id+"F11",true);
            extrude(context, id + "F12", {"entities" : qUnion([Q0]), "oppositeDirection" : true, "depth" : 40 * mm});
        }
        {
            var Q0;
            Q0=makeQuery(id+"F12.opExtrude","SWEPT_FACE",FACE,{"disambiguationData":[OSD([sQuery(id+"F11.wireOp",EDGE,"E131.top")])]});
            var sketch = newSketch(context, id + "F13", { "sketchPlane" : qUnion([Q0])});
            skCircle(sketch, "E138", {"center": v(40, 450) * mm, "radius": 5 * mm});
            skPoint(sketch, "E138.centerSnap0", {"position": v(40, 470) * mm});
            skSolve(sketch);
        }
        {
            var Q0;
            Q0=qSketchRegion(id+"F13",true);
            extrude(context, id + "F14", {"entities" : qUnion([Q0]), "operationType" : NewBodyOperationType.REMOVE, "oppositeDirection" : true, "depth" : 10 * mm});
        }
        {
            var Q0;
            Q0=makeQuery(id+"F12.opExtrude","SWEPT_FACE",FACE,{"disambiguationData":[OSD([sQuery(id+"F11.wireOp",EDGE,"E131.top")])]});
            var sketch = newSketch(context, id + "F15", { "sketchPlane" : qUnion([Q0])});
            skLineSegment(sketch, "E139.bottom", {"start": v(30, 362.1) * mm, "end": v(50, 362.1) * mm});
            skLineSegment(sketch, "E139.top", {"start": v(30, 312.1) * mm, "end": v(50, 312.1) * mm});
            skLineSegment(sketch, "E139.left", {"start": v(30, 362.1) * mm, "end": v(30, 312.1) * mm});
            skLineSegment(sketch, "E139.right", {"start": v(50, 362.1) * mm, "end": v(50, 312.1) * mm});
            skPoint(sketch, "E139.middle", {"position": v(40, 337.1) * mm});
            skPoint(sketch, "E139.middle.positionSnap0", {"position": v(40, 470) * mm});
            skPoint(sketch, "E139.centerSnap0", {"position": v(40, 470) * mm});
            skLineSegment(sketch, "E140", {"start": v(30, 362.1) * mm, "end": v(40, 350.1) * mm});
            skLineSegment(sketch, "E141", {"start": v(40, 350.1) * mm, "end": v(50, 362.1) * mm});
            skLineSegment(sketch, "E142", {"start": v(30, 312.1) * mm, "end": v(40, 324.1) * mm});
            skPoint(sketch, "E142.endSnap0", {"position": v(40, 312.1) * mm});
            skLineSegment(sketch, "E143", {"start": v(40, 324.1) * mm, "end": v(50, 312.1) * mm});
            skSolve(sketch);
        }
        {
            var Q0;
            Q0=makeQuery(id+"F15.imprint","IMPRINT",FACE,{"disambiguationData":[TD([[makeQuery(id+"F15.imprint","IMPRINT",EDGE,{"derivedFrom":sQuery(id+"F15.wireOp",EDGE,"E139.left")}),1.0]])]});
            extrude(context, id + "F16", {"entities" : qUnion([Q0]), "operationType" : NewBodyOperationType.REMOVE, "oppositeDirection" : true, "depth" : 10 * mm});
        }
        {
            var Q0;
            Q0=makeQuery(id+"F12.opExtrude","SWEPT_FACE",FACE,{"disambiguationData":[OSD([sQuery(id+"F11.wireOp",EDGE,"E133")])]});
            var sketch = newSketch(context, id + "F17", { "sketchPlane" : qUnion([Q0])});
            skLineSegment(sketch, "E144.bottom", {"start": v(30, 75) * mm, "end": v(50, 75) * mm});
            skLineSegment(sketch, "E144.top", {"start": v(30, 25) * mm, "end": v(50, 25) * mm});
            skLineSegment(sketch, "E144.left", {"start": v(30, 75) * mm, "end": v(30, 25) * mm});
            skLineSegment(sketch, "E144.right", {"start": v(50, 75) * mm, "end": v(50, 25) * mm});
            skPoint(sketch, "E144.middle", {"position": v(40, 50) * mm});
            skPoint(sketch, "E144.middle.positionSnap0", {"position": v(40, 0) * mm});
            skPoint(sketch, "E144.centerSnap0", {"position": v(40, 0) * mm});
            skLineSegment(sketch, "E145", {"start": v(30, 75) * mm, "end": v(40, 69) * mm});
            skPoint(sketch, "E145.endSnap0", {"position": v(40, 25) * mm});
            skLineSegment(sketch, "E146", {"start": v(40, 69) * mm, "end": v(50, 75) * mm});
            skLineSegment(sketch, "E147", {"start": v(30, 25) * mm, "end": v(40, 31) * mm});
            skLineSegment(sketch, "E148", {"start": v(40, 31) * mm, "end": v(50, 25) * mm});
            skSolve(sketch);
        }
        {
            var Q0;
            Q0=makeQuery(id+"F17.imprint","IMPRINT",FACE,{"disambiguationData":[TD([[makeQuery(id+"F17.imprint","IMPRINT",EDGE,{"derivedFrom":sQuery(id+"F17.wireOp",EDGE,"E144.left")}),1.0]])]});
            extrude(context, id + "F18", {"entities" : qUnion([Q0]), "operationType" : NewBodyOperationType.REMOVE, "oppositeDirection" : true, "depth" : 10 * mm});
        }
        {
            var Q0;
            Q0=makeQuery(id+"F12.opExtrude","SWEPT_FACE",FACE,{"disambiguationData":[OSD([sQuery(id+"F11.wireOp",EDGE,"E131.top")])]});
            var sketch = newSketch(context, id + "F19", { "sketchPlane" : qUnion([Q0])});
            skLineSegment(sketch, "E149", {"start": v(40, 350.1) * mm, "end": v(40, 375.1) * mm});
            skLineSegment(sketch, "E150", {"start": v(40, 375.1) * mm, "end": v(40.25, 375.1) * mm});
            skLineSegment(sketch, "E151", {"start": v(40.25, 375.1) * mm, "end": v(40.25, 350.4) * mm});
            skLineSegment(sketch, "E152", {"start": v(40, 375.1) * mm, "end": v(39.75, 375.1) * mm});
            skLineSegment(sketch, "E153", {"start": v(39.75, 375.1) * mm, "end": v(39.75, 350.4) * mm});
            skLineSegment(sketch, "E154", {"start": v(39.75, 350.4) * mm, "end": v(40, 350.1) * mm});
            skLineSegment(sketch, "E155", {"start": v(40.25, 350.4) * mm, "end": v(40, 350.1) * mm});
            skLineSegment(sketch, "E156", {"start": v(40, 324.1) * mm, "end": v(40, 299.1) * mm});
            skLineSegment(sketch, "E157", {"start": v(40, 299.1) * mm, "end": v(40.25, 299.1) * mm});
            skLineSegment(sketch, "E158", {"start": v(40.25, 299.1) * mm, "end": v(40.25, 323.8) * mm});
            skLineSegment(sketch, "E159", {"start": v(40.25, 323.8) * mm, "end": v(40, 324.1) * mm});
            skLineSegment(sketch, "E160", {"start": v(40, 299.1) * mm, "end": v(39.75, 299.1) * mm});
            skLineSegment(sketch, "E161", {"start": v(39.75, 299.1) * mm, "end": v(39.75, 323.8) * mm});
            skLineSegment(sketch, "E162", {"start": v(39.75, 323.8) * mm, "end": v(40, 324.1) * mm});
            skSolve(sketch);
        }
        {
            var Q0;
            Q0=qSketchRegion(id+"F19",true);
            extrude(context, id + "F20", {"entities" : qUnion([Q0]), "operationType" : NewBodyOperationType.REMOVE, "oppositeDirection" : true, "depth" : 0.5 * mm});
        }
        {
            var Q0;
            Q0=makeQuery(id+"F12.opExtrude","SWEPT_FACE",FACE,{"disambiguationData":[OSD([sQuery(id+"F11.wireOp",EDGE,"E133")])]});
            var sketch = newSketch(context, id + "F21", { "sketchPlane" : qUnion([Q0])});
            skLineSegment(sketch, "E163", {"start": v(40, 69) * mm, "end": v(40, 79) * mm});
            skLineSegment(sketch, "E164", {"start": v(40, 79) * mm, "end": v(40.25, 79) * mm});
            skLineSegment(sketch, "E165", {"start": v(40.25, 79) * mm, "end": v(40.25, 69.15) * mm});
            skLineSegment(sketch, "E166", {"start": v(40.25, 69.15) * mm, "end": v(40, 69) * mm});
            skLineSegment(sketch, "E167", {"start": v(40, 79) * mm, "end": v(39.75, 79) * mm});
            skLineSegment(sketch, "E168", {"start": v(39.75, 79) * mm, "end": v(39.75, 69.15) * mm});
            skLineSegment(sketch, "E169", {"start": v(39.75, 69.15) * mm, "end": v(40, 69) * mm});
            skLineSegment(sketch, "E170", {"start": v(40, 31) * mm, "end": v(40, 21) * mm});
            skLineSegment(sketch, "E171", {"start": v(40, 21) * mm, "end": v(40.25, 21) * mm});
            skLineSegment(sketch, "E172", {"start": v(40.25, 21) * mm, "end": v(40.25, 30.85) * mm});
            skLineSegment(sketch, "E173", {"start": v(40.25, 30.85) * mm, "end": v(40, 31) * mm});
            skLineSegment(sketch, "E174", {"start": v(40, 21) * mm, "end": v(39.75, 21) * mm});
            skLineSegment(sketch, "E175", {"start": v(39.75, 21) * mm, "end": v(39.75, 30.85) * mm});
            skLineSegment(sketch, "E176", {"start": v(39.75, 30.85) * mm, "end": v(40, 31) * mm});
            skSolve(sketch);
        }
        {
            var Q0;
            Q0=qSketchRegion(id+"F21",true);
            extrude(context, id + "F22", {"entities" : qUnion([Q0]), "operationType" : NewBodyOperationType.REMOVE, "oppositeDirection" : true, "depth" : 0.25 * mm});
        }
        {
            var Q0;
            Q0=makeQuery(id+"F1.opExtrude","SWEPT_EDGE",EDGE,{"disambiguationData":[OSD([sQuery(id+"F0.wireOp",EDGE,"E33"),sQuery(id+"F0.wireOp",EDGE,"E34")])]});
            var Q1;
            Q1=makeQuery(id+"F1.opExtrude","SWEPT_EDGE",EDGE,{"disambiguationData":[OSD([sQuery(id+"F0.wireOp",EDGE,"E29"),sQuery(id+"F0.wireOp",EDGE,"E30")])]});
            fillet(context, id + "F23", {"entities" : qUnion([Q0, Q1]), "radius" : 50 * mm, "tangentPropagation" : true, "allowEdgeOverflow" : false});
        }
        {
            var Q0;
            Q0=makeQuery(id+"F1.opExtrude","SWEPT_EDGE",EDGE,{"disambiguationData":[OSD([sQuery(id+"F0.wireOp",EDGE,"E27"),sQuery(id+"F0.wireOp",EDGE,"E28")])]});
            var Q1;
            Q1=makeQuery(id+"F1.opExtrude","SWEPT_EDGE",EDGE,{"disambiguationData":[OSD([sQuery(id+"F0.wireOp",EDGE,"E32"),sQuery(id+"F0.wireOp",EDGE,"E33")])]});
            var Q2;
            Q2=makeQuery(id+"F1.opExtrude","SWEPT_EDGE",EDGE,{"disambiguationData":[OSD([sQuery(id+"F0.wireOp",EDGE,"E23"),sQuery(id+"F0.wireOp",EDGE,"E24")])]});
            fillet(context, id + "F24", {"entities" : qUnion([Q0, Q1, Q2]), "radius" : 20 * mm, "tangentPropagation" : true, "allowEdgeOverflow" : false});
        }
        {
            var Q0;
            Q0=makeQuery(id+"F12.opExtrude","CAP_EDGE",EDGE,{"disambiguationData":[OSD([sQuery(id+"F11.wireOp",EDGE,"E134")])],"isStart":true});
            var Q1;
            Q1=makeQuery(id+"F12.opExtrude","CAP_EDGE",EDGE,{"disambiguationData":[OSD([sQuery(id+"F11.wireOp",EDGE,"E134")])],"isStart":false});
            var Q2;
            Q2=makeQuery(id+"F12.opExtrude","CAP_EDGE",EDGE,{"disambiguationData":[OSD([sQuery(id+"F11.wireOp",EDGE,"E131.left")])],"isStart":false});
            var Q3;
            Q3=makeQuery(id+"F12.opExtrude","CAP_EDGE",EDGE,{"disambiguationData":[OSD([sQuery(id+"F11.wireOp",EDGE,"E131.left")])],"isStart":true});
            fillet(context, id + "F25", {"entities" : qUnion([Q0, Q1, Q2, Q3]), "radius" : 20 * mm, "tangentPropagation" : true, "allowEdgeOverflow" : false});
        }
        {
            var Q0;
            Q0=makeQuery(id+"F12.opExtrude","SWEPT_EDGE",EDGE,{"disambiguationData":[OSD([sQuery(id+"F11.wireOp",EDGE,"E132"),sQuery(id+"F11.wireOp",EDGE,"E133")])]});
            var Q1;
            Q1=makeQuery(id+"F12.opExtrude","SWEPT_EDGE",EDGE,{"disambiguationData":[OSD([sQuery(id+"F11.wireOp",EDGE,"E131.bottom"),sQuery(id+"F11.wireOp",EDGE,"E136")])]});
            fillet(context, id + "F26", {"entities" : qUnion([Q0, Q1]), "radius" : 10 * mm, "tangentPropagation" : true, "allowEdgeOverflow" : false});
        }
        {
            var Q0;
            Q0=makeQuery(id+"F12.opExtrude","SWEPT_EDGE",EDGE,{"disambiguationData":[OSD([sQuery(id+"F11.wireOp",EDGE,"E131.top"),sQuery(id+"F11.wireOp",EDGE,"E132")])]});
            var Q1;
            Q1=makeQuery(id+"F12.opExtrude","SWEPT_EDGE",EDGE,{"disambiguationData":[OSD([sQuery(id+"F11.wireOp",EDGE,"E135"),sQuery(id+"F11.wireOp",EDGE,"E136")])]});
            fillet(context, id + "F27", {"entities" : qUnion([Q0, Q1]), "radius" : 5 * mm, "tangentPropagation" : true, "allowEdgeOverflow" : false});
        }
        {
            var Q0;
            Q0=qCreatedBy(makeId("Right.planeOp"),FACE);
            var sketch = newSketch(context, id + "F28", { "sketchPlane" : qUnion([Q0])});
            skArc(sketch, "E177", {"start": v(-47.48, 41.9) * mm, "mid": v(-68.98, 63.4) * mm, "end": v(-90.48, 41.9) * mm});
            skLineSegment(sketch, "E178", {"start": v(-47.48, 41.9) * mm, "end": v(-47.48, 20.4) * mm});
            skLineSegment(sketch, "E179", {"start": v(-90.48, 41.9) * mm, "end": v(-90.48, 20.4) * mm});
            skSolve(sketch);
        }
        {
            var Q0;
            Q0=sQuery(id+"F28.wireOp",VERTEX,"E179.end");
            var Q1;
            Q1=qCreatedBy(makeId("Top.planeOp"),FACE);
            cPlane(context, id + "F29", {"entities" : qUnion([Q0, Q1]), "cplaneType" : CPlaneType.PLANE_POINT, "offset" : 25 * mm, "width" : 150 * mm, "height" : 150 * mm});
        }
        {
            var Q0;
            Q0=qCreatedBy(id+"F29.planeOp",FACE);
            var sketch = newSketch(context, id + "F30", { "sketchPlane" : qUnion([Q0])});
            skCircle(sketch, "E180", {"center": v(0, -90.48) * mm, "radius": 5 * mm});
            skSolve(sketch);
        }
        {
            var Q0;
            Q0=makeQuery(id+"F30.imprint","IMPRINT",FACE,{"disambiguationData":[TD([[makeQuery(id+"F30.imprint","IMPRINT",EDGE,{"derivedFrom":sQuery(id+"F30.wireOp",EDGE,"E180")}),1.0]])]});
            var Q1;
            Q1=sQuery(id+"F28.wireOp",EDGE,"E179");
            var Q2;
            Q2=sQuery(id+"F28.wireOp",EDGE,"E177");
            var Q3;
            Q3=sQuery(id+"F28.wireOp",EDGE,"E178");
            sweep(context, id + "F31", {"profiles" : qUnion([Q0]), "path" : qUnion([Q1, Q2, Q3])});
        }
        {
            var Q0;
            Q0=qCreatedBy(makeId("Right.planeOp"),FACE);
            var sketch = newSketch(context, id + "F32", { "sketchPlane" : qUnion([Q0])});
            skLineSegment(sketch, "E181", {"start": v(-114.2, 20.99) * mm, "end": v(-139.2, 20.99) * mm});
            skArc(sketch, "E182", {"start": v(-139.2, 40.56) * mm, "mid": v(-158.2, 59.56) * mm, "end": v(-177.2, 40.56) * mm});
            skArc(sketch, "E183.0", {"start": v(-134.2, 40.56) * mm, "mid": v(-158.2, 64.56) * mm, "end": v(-182.2, 40.56) * mm});
            skLineSegment(sketch, "E184.left", {"start": v(-139.2, 40.56) * mm, "end": v(-139.2, 20.99) * mm});
            skLineSegment(sketch, "E184.right", {"start": v(-134.2, 40.56) * mm, "end": v(-134.2, 26.56) * mm});
            skLineSegment(sketch, "E185.left", {"start": v(-177.2, 40.56) * mm, "end": v(-177.2, 20.99) * mm});
            skLineSegment(sketch, "E185.right", {"start": v(-182.2, 40.56) * mm, "end": v(-182.2, 26.56) * mm});
            skLineSegment(sketch, "E186", {"start": v(-134.2, 26.56) * mm, "end": v(-114.2, 26.56) * mm});
            skLineSegment(sketch, "E187", {"start": v(-114.2, 26.56) * mm, "end": v(-114.2, 20.99) * mm});
            skLineSegment(sketch, "E188", {"start": v(-182.2, 26.56) * mm, "end": v(-202.2, 26.56) * mm});
            skLineSegment(sketch, "E189", {"start": v(-202.2, 26.56) * mm, "end": v(-202.2, 20.99) * mm});
            skPoint(sketch, "E190.orphan", {"position": v(-139.2, 16.56) * mm});
            skLineSegment(sketch, "E191.trimOffspring", {"start": v(-177.2, 20.99) * mm, "end": v(-220.09, 20.99) * mm});
            skPoint(sketch, "E192.trimOffspring.end.orphan", {"position": v(-182.2, 16.56) * mm});
            skSolve(sketch);
        }
        {
            var Q0;
            Q0=qSketchRegion(id+"F32",true);
            extrude(context, id + "F33", {"entities" : qUnion([Q0]), "depth" : 25 * mm});
        }
        {
            var Q0;
            Q0=makeQuery(id+"F1.opExtrude","CAP_FACE",FACE,{"disambiguationData":[OSD([sQuery(id+"F0.wireOp",EDGE,"E3"),sQuery(id+"F0.wireOp",EDGE,"E4"),sQuery(id+"F0.wireOp",EDGE,"E14"),sQuery(id+"F0.wireOp",EDGE,"E20"),sQuery(id+"F0.wireOp",EDGE,"E23"),sQuery(id+"F0.wireOp",EDGE,"E24"),sQuery(id+"F0.wireOp",EDGE,"E27"),sQuery(id+"F0.wireOp",EDGE,"E28"),sQuery(id+"F0.wireOp",EDGE,"E29"),sQuery(id+"F0.wireOp",EDGE,"E30"),sQuery(id+"F0.wireOp",EDGE,"E32"),sQuery(id+"F0.wireOp",EDGE,"E33"),sQuery(id+"F0.wireOp",EDGE,"E34")])],"isStart":false});
            var sketch = newSketch(context, id + "F34", { "sketchPlane" : qUnion([Q0])});
            skCircle(sketch, "E193", {"center": v(423.87, 419.16) * mm, "radius": 10 * mm});
            skCircle(sketch, "E194", {"center": v(493.87, 419.16) * mm, "radius": 10 * mm});
            skCircle(sketch, "E195", {"center": v(397.32, 292.18) * mm, "radius": 10 * mm});
            skCircle(sketch, "E196", {"center": v(461.34, 263.86) * mm, "radius": 10 * mm});
            skLineSegment(sketch, "E197", {"start": v(493.87, 429.16) * mm, "end": v(423.87, 429.16) * mm});
            skLineSegment(sketch, "E198", {"start": v(423.87, 409.16) * mm, "end": v(493.87, 409.16) * mm});
            skLineSegment(sketch, "E199", {"start": v(393.27, 283.03) * mm, "end": v(457.3, 254.72) * mm});
            skLineSegment(sketch, "E200", {"start": v(457.3, 254.72) * mm, "end": v(465.38, 273) * mm});
            skLineSegment(sketch, "E201", {"start": v(465.38, 273) * mm, "end": v(401.48, 301.27) * mm});
            skSolve(sketch);
        }
        {
            var Q0;
            Q0=qSketchRegion(id+"F34",true);
            extrude(context, id + "F35", {"entities" : qUnion([Q0]), "operationType" : NewBodyOperationType.REMOVE, "oppositeDirection" : true, "depth" : 3 * mm});
        }
    });
